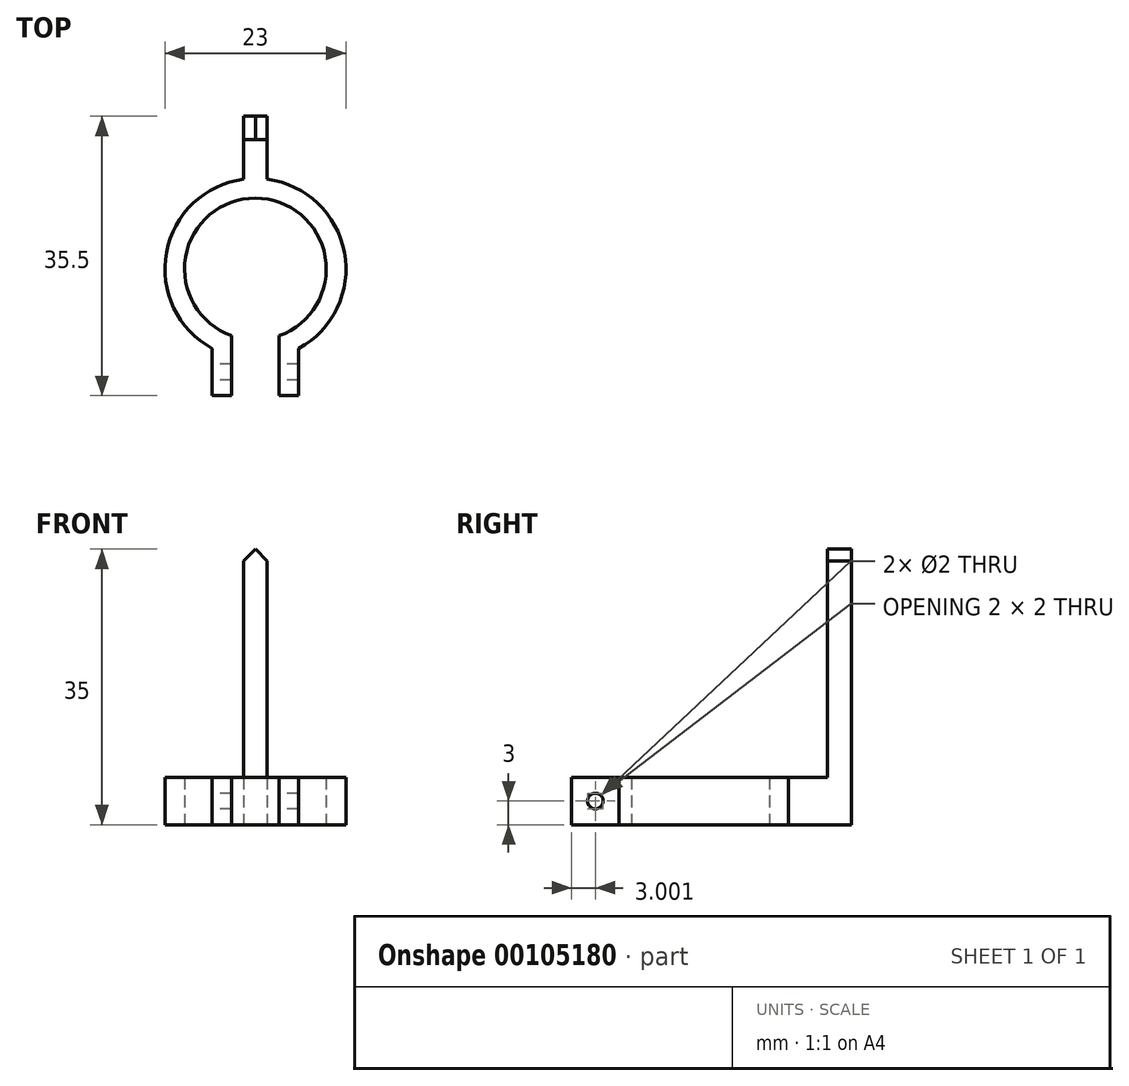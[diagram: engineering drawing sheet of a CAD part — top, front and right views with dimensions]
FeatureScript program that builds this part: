
annotation { "Feature Type Name" : "Feature", "Feature Type Description" : "" }
export const myFeature = defineFeature(function(context is Context, id is Id, definition is map)
    precondition{}
    {
        {
            var Q0;
            Q0=qCreatedBy(makeId("Top.planeOp"),FACE);
            var sketch = newSketch(context, id + "F0", { "sketchPlane" : qUnion([Q0])});
            skCircle(sketch, "E0", {"center": v(0, 0) * mm, "radius": 9 * mm});
            skCircle(sketch, "E1", {"center": v(0, 0) * mm, "radius": 11.5 * mm});
            skLineSegment(sketch, "E2", {"start": v(3, -8.49) * mm, "end": v(3, -11.1) * mm});
            skLineSegment(sketch, "E3.MirrorCS", {"start": v(-3, -8.49) * mm, "end": v(-3, -11.1) * mm});
            skLineSegment(sketch, "E4", {"start": v(3, -11.1) * mm, "end": v(3, -16.1) * mm});
            skLineSegment(sketch, "E5", {"start": v(3, -16.1) * mm, "end": v(5.5, -16.1) * mm});
            skLineSegment(sketch, "E6", {"start": v(5.5, -16.1) * mm, "end": v(5.5, -10.1) * mm});
            skLineSegment(sketch, "E7.MirrorCS", {"start": v(-5.5, -16.1) * mm, "end": v(-5.5, -10.1) * mm});
            skLineSegment(sketch, "E8.MirrorCS", {"start": v(-3, -16.1) * mm, "end": v(-5.5, -16.1) * mm});
            skLineSegment(sketch, "E9.MirrorCS", {"start": v(-3, -11.1) * mm, "end": v(-3, -16.1) * mm});
            skLineSegment(sketch, "E10", {"start": v(-1.5, 11.4) * mm, "end": v(-1.5, 19.4) * mm});
            skLineSegment(sketch, "E11.MirrorCS", {"start": v(1.5, 11.4) * mm, "end": v(1.5, 19.4) * mm});
            skLineSegment(sketch, "E12", {"start": v(-1.5, 19.4) * mm, "end": v(1.5, 19.4) * mm});
            skSolve(sketch);
        }
        {
            var Q0;
            {var subQ3=sQuery(id+"F0.wireOp",EDGE,"E2");Q0=makeQuery(id+"F0.imprint","IMPRINT",FACE,{"disambiguationData":[TD([[makeQuery(id+"F0.imprint","IMPRINT",EDGE,{"derivedFrom":subQ3}),1.0]])]});}
            var Q1;
            {var subQ0=sQuery(id+"F0.wireOp",EDGE,"E4");Q1=makeQuery(id+"F0.imprint","IMPRINT",FACE,{"disambiguationData":[TD([[makeQuery(id+"F0.imprint","IMPRINT",EDGE,{"derivedFrom":subQ0}),1.0]])]});}
            var Q2;
            {var subQ2=sQuery(id+"F0.wireOp",EDGE,"E7.MirrorCS");Q2=makeQuery(id+"F0.imprint","IMPRINT",FACE,{"disambiguationData":[TD([[makeQuery(id+"F0.imprint","IMPRINT",EDGE,{"derivedFrom":subQ2}),-1.0]])]});}
            var Q3;
            {var subQ0=sQuery(id+"F0.wireOp",EDGE,"E10");Q3=makeQuery(id+"F0.imprint","IMPRINT",FACE,{"disambiguationData":[TD([[makeQuery(id+"F0.imprint","IMPRINT",EDGE,{"derivedFrom":subQ0}),-1.0]])]});}
            extrude(context, id + "F1", {"entities" : qUnion([Q0, Q1, Q2, Q3]), "depth" : 6 * mm});
        }
        {
            var Q0;
            Q0=makeQuery(id+"F1.opExtrude","CAP_FACE",FACE,{"disambiguationData":[OSD([sQuery(id+"F0.wireOp",EDGE,"E0"),sQuery(id+"F0.wireOp",EDGE,"E1"),sQuery(id+"F0.wireOp",EDGE,"E2"),sQuery(id+"F0.wireOp",EDGE,"E3.MirrorCS"),sQuery(id+"F0.wireOp",EDGE,"E4"),sQuery(id+"F0.wireOp",EDGE,"E5"),sQuery(id+"F0.wireOp",EDGE,"E6"),sQuery(id+"F0.wireOp",EDGE,"E7.MirrorCS"),sQuery(id+"F0.wireOp",EDGE,"E8.MirrorCS"),sQuery(id+"F0.wireOp",EDGE,"E9.MirrorCS"),sQuery(id+"F0.wireOp",EDGE,"E10"),sQuery(id+"F0.wireOp",EDGE,"E11.MirrorCS"),sQuery(id+"F0.wireOp",EDGE,"E12")])],"isStart":false});
            var sketch = newSketch(context, id + "F2", { "sketchPlane" : qUnion([Q0])});
            skArc(sketch, "E13.0.0", {"start": v(5.5, -10.1) * mm, "mid": v(11.3, 2.1) * mm, "end": v(1.5, 11.4) * mm});
            skLineSegment(sketch, "E13.0.1", {"start": v(1.5, 11.4) * mm, "end": v(1.5, 19.4) * mm});
            skLineSegment(sketch, "E13.0.2", {"start": v(1.5, 19.4) * mm, "end": v(-1.5, 19.4) * mm});
            skLineSegment(sketch, "E13.0.3", {"start": v(-1.5, 19.4) * mm, "end": v(-1.5, 11.4) * mm});
            skArc(sketch, "E13.0.4", {"start": v(-1.5, 11.4) * mm, "mid": v(-11.3, 2.1) * mm, "end": v(-5.5, -10.1) * mm});
            skLineSegment(sketch, "E13.0.5", {"start": v(-5.5, -10.1) * mm, "end": v(-5.5, -16.1) * mm});
            skLineSegment(sketch, "E13.0.6", {"start": v(-5.5, -16.1) * mm, "end": v(-3, -16.1) * mm});
            skLineSegment(sketch, "E13.0.7", {"start": v(-3, -16.1) * mm, "end": v(-3, -8.49) * mm});
            skArc(sketch, "E13.0.8", {"start": v(-3, -8.49) * mm, "mid": v(0, 9) * mm, "end": v(3, -8.49) * mm});
            skLineSegment(sketch, "E13.0.9", {"start": v(3, -8.49) * mm, "end": v(3, -16.1) * mm});
            skLineSegment(sketch, "E13.0.10", {"start": v(3, -16.1) * mm, "end": v(5.5, -16.1) * mm});
            skLineSegment(sketch, "E13.0.11", {"start": v(5.5, -16.1) * mm, "end": v(5.5, -10.1) * mm});
            skLineSegment(sketch, "E14", {"start": v(-1.5, 16.4) * mm, "end": v(1.5, 16.4) * mm});
            skSolve(sketch);
        }
        {
            var Q0;
            {var subQ0=sQuery(id+"F2.wireOp",EDGE,"E13.0.2");Q0=makeQuery(id+"F2.imprint","IMPRINT",FACE,{"disambiguationData":[TD([[makeQuery(id+"F2.imprint","IMPRINT",EDGE,{"derivedFrom":subQ0}),-1.0]])]});}
            extrude(context, id + "F3", {"entities" : qUnion([Q0]), "operationType" : NewBodyOperationType.ADD, "depth" : 29 * mm});
        }
        {
            var Q0;
            Q0=makeQuery(id+"F1.opExtrude","SWEPT_FACE",FACE,{"disambiguationData":[OSD([sQuery(id+"F0.wireOp",EDGE,"E7.MirrorCS")])]});
            var sketch = newSketch(context, id + "F4", { "sketchPlane" : qUnion([Q0])});
            skLineSegment(sketch, "E15.0.0", {"start": v(10.1, 0) * mm, "end": v(16.1, 0) * mm});
            skLineSegment(sketch, "E15.0.1", {"start": v(16.1, 0) * mm, "end": v(16.1, 6) * mm});
            skLineSegment(sketch, "E15.0.2", {"start": v(16.1, 6) * mm, "end": v(10.1, 6) * mm});
            skLineSegment(sketch, "E15.0.3", {"start": v(10.1, 6) * mm, "end": v(10.1, 0) * mm});
            skPoint(sketch, "E16", {"position": v(16.1, 3) * mm});
            skPoint(sketch, "E17", {"position": v(13.1, 6) * mm});
            skPoint(sketch, "E18", {"position": v(13.1, 3) * mm});
            skSolve(sketch);
        }
        {
            var Q0;
            Q0=sQuery(id+"F4.wireOp",VERTEX,"E18");
            var Q1;
            Q1=makeQuery(id+"F1.opExtrude","SWEPT_BODY",BODY,{"disambiguationData":[OSD([sQuery(id+"F0.wireOp",EDGE,"E0"),sQuery(id+"F0.wireOp",EDGE,"E1"),sQuery(id+"F0.wireOp",EDGE,"E2"),sQuery(id+"F0.wireOp",EDGE,"E3.MirrorCS"),sQuery(id+"F0.wireOp",EDGE,"E4"),sQuery(id+"F0.wireOp",EDGE,"E5"),sQuery(id+"F0.wireOp",EDGE,"E6"),sQuery(id+"F0.wireOp",EDGE,"E7.MirrorCS"),sQuery(id+"F0.wireOp",EDGE,"E8.MirrorCS"),sQuery(id+"F0.wireOp",EDGE,"E9.MirrorCS"),sQuery(id+"F0.wireOp",EDGE,"E10"),sQuery(id+"F0.wireOp",EDGE,"E11.MirrorCS"),sQuery(id+"F0.wireOp",EDGE,"E12")])]});
            hole(context, id + "F5", {"style" : HoleStyle.SIMPLE, "endStyle" : HoleEndStyle.THROUGH, "holeDiameter" : 2 * mm, "locations" : qUnion([Q0]), "scope" : qUnion([Q1]), "isTappedThrough" : true});
        }
        {
            var Q0;
            Q0=makeQuery(id+"F3.opExtrude","CAP_EDGE",EDGE,{"disambiguationData":[OSD([sQuery(id+"F2.wireOp",EDGE,"E13.0.1")])],"isStart":false});
            var Q1;
            Q1=makeQuery(id+"F3.opExtrude","CAP_EDGE",EDGE,{"disambiguationData":[OSD([sQuery(id+"F2.wireOp",EDGE,"E13.0.3")])],"isStart":false});
            chamfer(context, id + "F6", {"entities" : qUnion([Q0, Q1]), "width" : 1.5 * mm, "tangentPropagation" : true});
        }
    });
